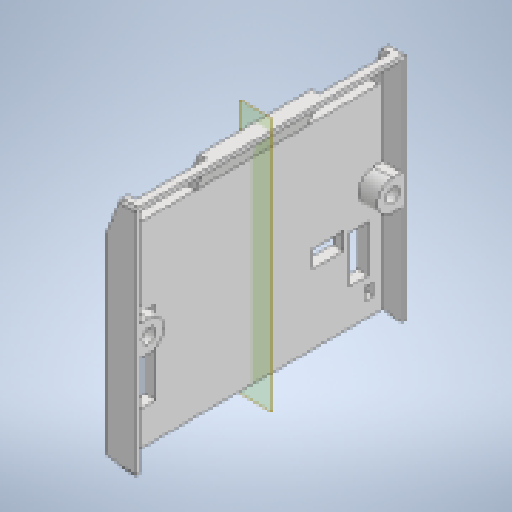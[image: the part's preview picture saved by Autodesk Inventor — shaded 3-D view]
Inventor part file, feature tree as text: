
AUTODESK INVENTOR PART (.ipt)
format: ipt  version: 2023.5 (Build 275446000, 446)  size: 477,184 bytes
history: native  units: mm
features: extrude x16, sketch x15, projected_geometry x13, reference x12, other x5, mirror x1
ambient origin geometry x8: Origin, YZ Plane, XZ Plane, XY Plane, X Axis, Y Axis, Z Axis, Center Point
bodies: Body1 (feature_tree), Body2 (feature_tree)
feature tree (62):
  other  "Bryła1"
  extrude  "Wyciągnięcie proste1"  Depth=4.0mm TaperAngle=0.0deg
  sketch  "Szkic2"
  extrude  "Wyciągnięcie proste2"  TaperAngle=0.0deg  [1 undecoded]
  extrude  "Wyciągnięcie proste3"  Depth=10.0mm TaperAngle=0.0deg
  extrude  "Wyciągnięcie proste5"  Depth=0.8mm
  extrude  "Wyciągnięcie proste6"  Depth=1.5mm
  extrude  "Wyciągnięcie proste9"  Depth=1.5mm
  extrude  "Wyciągnięcie proste10"  Depth=2.0mm TaperAngle=0.0deg
  extrude  "Wyciągnięcie proste11"  Depth=1.5mm TaperAngle=0.0deg
  extrude  "Wyciągnięcie proste12"  Depth=13.0mm
  other  "Płaszczyzna konstrukcyjna1"
  mirror  "Odbij1"
  extrude  "Wyciągnięcie proste13"  Depth=13.0mm
  extrude  "Wyciągnięcie proste14"  Depth=1.6mm
  extrude  "Wyciągnięcie proste15"  Depth=1.6mm
  extrude  "Wyciągnięcie proste16"  Depth=6.0mm
  extrude  "Wyciągnięcie proste17"  Depth=4.0mm TaperAngle=0.0deg
  extrude  "Wyciągnięcie proste18"  Depth=4.0mm TaperAngle=0.0deg
  extrude  "Wyciągnięcie proste19"  Depth=1.6mm
  sketch  "Szkic1"
  projected_geometry  "Pętla rzutowana1"
  sketch  "Szkic4"
  projected_geometry  "Pętla rzutowana4"
  sketch  "Szkic5"
  projected_geometry  "Pętla rzutowana5"
  sketch  "Szkic9"
  projected_geometry  "Pętla rzutowana10"
  sketch  "Szkic10"
  projected_geometry  "Pętla rzutowana11"
  sketch  "Szkic11"
  projected_geometry  "Pętla rzutowana12"
  projected_geometry  "Pętla rzutowana13"
  sketch  "Szkic12"
  projected_geometry  "Pętla rzutowana14"
  sketch  "Szkic13"
  projected_geometry  "Pętla rzutowana15"
  projected_geometry  "Pętla rzutowana16"
  projected_geometry  "Pętla rzutowana17"
  sketch  "Szkic14"
  reference  "Odniesienie4"
  reference  "Odniesienie5"
  reference  "Odniesienie6"
  reference  "Odniesienie7"
  sketch  "Szkic15"
  sketch  "Szkic16"
  sketch  "Szkic17"
  projected_geometry  "Pętla rzutowana18"
  sketch  "Szkic18"
  reference  "Odniesienie8"
  reference  "Odniesienie9"
  reference  "Odniesienie10"
  reference  "Odniesienie11"
  sketch  "Szkic19"
  reference  "Odniesienie12"
  reference  "Odniesienie13"
  projected_geometry  "Pętla rzutowana19"
  reference  "Odniesienie14"
  reference  "Odniesienie15"
  parser-record x1  (decoder bookkeeping rows leaked as tree rows — omitted from the tree; the rows remain in map.json)
  other  "stratos_v2_mechanics.iam"
  other  "MikroSumo:1"
note: 1 required parameter value undecoded (feature->parameter linkage not recoverable at this tier; creation-order binding heuristic only, values carry confidence <= 0.55)
note: 1 file-system path scrubbed to <path> (originals preserved in map.json)
